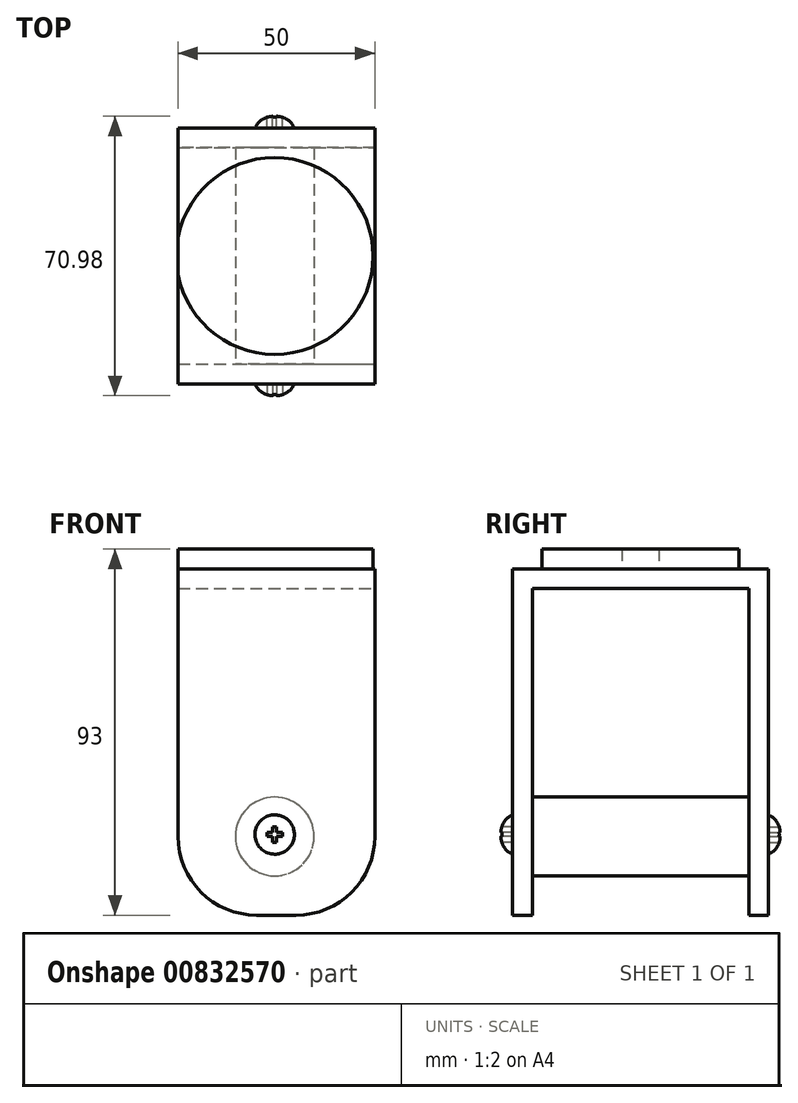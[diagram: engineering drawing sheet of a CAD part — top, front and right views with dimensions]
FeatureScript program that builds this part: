
annotation { "Feature Type Name" : "Feature", "Feature Type Description" : "" }
export const myFeature = defineFeature(function(context is Context, id is Id, definition is map)
    precondition{}
    {
        {
            var Q0;
            Q0=qCreatedBy(makeId("Front.planeOp"),FACE);
            var sketch = newSketch(context, id + "F0", { "sketchPlane" : qUnion([Q0])});
            skLineSegment(sketch, "E0.bottom", {"start": v(-24.56, 36.04) * mm, "end": v(25.44, 36.04) * mm});
            skLineSegment(sketch, "E0.top", {"start": v(-4.56, -46.96) * mm, "end": v(5.44, -46.96) * mm});
            skLineSegment(sketch, "E0.left", {"start": v(-24.56, 36.04) * mm, "end": v(-24.56, -26.96) * mm});
            skLineSegment(sketch, "E0.right", {"start": v(25.44, 36.04) * mm, "end": v(25.44, -26.96) * mm});
            skPoint(sketch, "E1.visualSharp", {"position": v(-24.56, -46.96) * mm});
            skArc(sketch, "E1.filletArc", {"start": v(-24.56, -26.96) * mm, "mid": v(-18.7, -41.1) * mm, "end": v(-4.56, -46.96) * mm});
            skPoint(sketch, "E2.visualSharp", {"position": v(25.44, -46.96) * mm});
            skArc(sketch, "E2.filletArc", {"start": v(5.44, -46.96) * mm, "mid": v(19.58, -41.1) * mm, "end": v(25.44, -26.96) * mm});
            skSolve(sketch);
        }
        {
            var Q0;
            Q0=makeQuery(id+"F0.imprint","IMPRINT",FACE,{"disambiguationData":[TD([[makeQuery(id+"F0.imprint","IMPRINT",EDGE,{"derivedFrom":sQuery(id+"F0.wireOp",EDGE,"E0.bottom")}),-1.0]])]});
            extrude(context, id + "F1", {"entities" : qUnion([Q0]), "depth" : 5 * mm, "offsetDistance" : 25 * mm});
        }
        {
            var Q0;
            Q0=makeQuery(id+"F1.opExtrude","SWEPT_FACE",FACE,{"disambiguationData":[OSD([sQuery(id+"F0.wireOp",EDGE,"E0.bottom")])]});
            var sketch = newSketch(context, id + "F2", { "sketchPlane" : qUnion([Q0])});
            skLineSegment(sketch, "E3.bottom", {"start": v(25.44, -5) * mm, "end": v(-24.56, -5) * mm});
            skLineSegment(sketch, "E3.top", {"start": v(25.44, 55) * mm, "end": v(-24.56, 55) * mm});
            skLineSegment(sketch, "E3.left", {"start": v(25.44, -5) * mm, "end": v(25.44, 55) * mm});
            skLineSegment(sketch, "E3.right", {"start": v(-24.56, -5) * mm, "end": v(-24.56, 55) * mm});
            skSolve(sketch);
        }
        {
            var Q0;
            {var subQ0=sQuery(id+"F2.wireOp",EDGE,"E3.top");Q0=makeQuery(id+"F2.imprint","IMPRINT",FACE,{"disambiguationData":[TD([[makeQuery(id+"F2.imprint","IMPRINT",EDGE,{"derivedFrom":subQ0}),1.0]])]});}
            var Q1;
            {var subQ0=sQuery(id+"F2.wireOp",EDGE,"E3.bottom");Q1=makeQuery(id+"F2.imprint","IMPRINT",FACE,{"disambiguationData":[TD([[makeQuery(id+"F2.imprint","IMPRINT",EDGE,{"derivedFrom":subQ0}),1.0]])]});}
            extrude(context, id + "F3", {"entities" : qUnion([Q0, Q1]), "operationType" : NewBodyOperationType.ADD, "depth" : 5 * mm, "offsetDistance" : 25 * mm});
        }
        {
            var Q0;
            Q0=makeQuery(id+"F1.opExtrude","CAP_FACE",FACE,{"disambiguationData":[OSD([sQuery(id+"F0.wireOp",EDGE,"E0.bottom"),sQuery(id+"F0.wireOp",EDGE,"E0.top"),sQuery(id+"F0.wireOp",EDGE,"E0.left"),sQuery(id+"F0.wireOp",EDGE,"E0.right"),sQuery(id+"F0.wireOp",EDGE,"E1.filletArc"),sQuery(id+"F0.wireOp",EDGE,"E2.filletArc")])],"isStart":true});
            cPlane(context, id + "F4", {"entities" : qUnion([Q0]), "cplaneType" : CPlaneType.OFFSET, "offset" : 27.5 * mm, "width" : 150 * mm, "height" : 150 * mm});
        }
        {
            var Q0;
            Q0=makeQuery(id+"F1.opExtrude","SWEPT_BODY",BODY,{"disambiguationData":[OSD([sQuery(id+"F0.wireOp",EDGE,"E0.bottom"),sQuery(id+"F0.wireOp",EDGE,"E0.top"),sQuery(id+"F0.wireOp",EDGE,"E0.left"),sQuery(id+"F0.wireOp",EDGE,"E0.right"),sQuery(id+"F0.wireOp",EDGE,"E1.filletArc"),sQuery(id+"F0.wireOp",EDGE,"E2.filletArc")])]});
            var Q1;
            Q1=qCreatedBy(id+"F4.planeOp",FACE);
            mirror(context, id + "F5", {"operationType" : NewBodyOperationType.ADD, "entities" : qUnion([Q0]), "mirrorPlane" : qUnion([Q1])});
        }
        {
            var Q0;
            {var subQ0=makeQuery(id+"F3.opExtrude","CAP_FACE",FACE,{"disambiguationData":[OSD([sQuery(id+"F2.wireOp",EDGE,"E3.bottom"),sQuery(id+"F2.wireOp",EDGE,"E3.top"),sQuery(id+"F2.wireOp",EDGE,"E3.left"),sQuery(id+"F2.wireOp",EDGE,"E3.right")])],"isStart":false});Q0=makeQuery(id+"F5.boolean.opBoolean","MERGE",FACE,{"derivedFrom":[subQ0,makeQuery(id+"F5.opPattern","COPY",FACE,{"derivedFrom":subQ0,"instanceName":"1"})]});}
            var sketch = newSketch(context, id + "F6", { "sketchPlane" : qUnion([Q0])});
            skCircle(sketch, "E4", {"center": v(0, 27.5) * mm, "radius": 25 * mm});
            skSolve(sketch);
        }
        {
            var Q0;
            {var subQ0=sQuery(id+"F6.wireOp",EDGE,"E4");var subQ1=makeQuery(id+"F3.opExtrude","CAP_EDGE",EDGE,{"disambiguationData":[OSD([sQuery(id+"F2.wireOp",EDGE,"E3.right")])],"isStart":false});var subQ2=makeQuery(id+"F5.boolean.opBoolean","MERGE",EDGE,{"derivedFrom":[subQ1,makeQuery(id+"F5.opPattern","COPY",EDGE,{"derivedFrom":subQ1,"instanceName":"1"})]});var subQ3=makeQuery(id+"F6.imprint","INTERSECT",VERTEX,{"disambiguationData":[OD(0.0)],"derivedFrom":[subQ2,subQ0]});Q0=makeQuery(id+"F6.imprint","IMPRINT",FACE,{"disambiguationData":[TD([[makeQuery(id+"F6.imprint","IMPRINT",EDGE,{"disambiguationData":[TD([[subQ3,-1.0]])],"derivedFrom":subQ0}),1.0]])]});}
            extrude(context, id + "F7", {"entities" : qUnion([Q0]), "operationType" : NewBodyOperationType.ADD, "depth" : 5 * mm, "offsetDistance" : 25 * mm});
        }
        {
            var Q0;
            Q0=makeQuery(id+"F1.opExtrude","CAP_FACE",FACE,{"disambiguationData":[OSD([sQuery(id+"F0.wireOp",EDGE,"E0.bottom"),sQuery(id+"F0.wireOp",EDGE,"E0.top"),sQuery(id+"F0.wireOp",EDGE,"E0.left"),sQuery(id+"F0.wireOp",EDGE,"E0.right"),sQuery(id+"F0.wireOp",EDGE,"E1.filletArc"),sQuery(id+"F0.wireOp",EDGE,"E2.filletArc")])],"isStart":true});
            var sketch = newSketch(context, id + "F8", { "sketchPlane" : qUnion([Q0])});
            skCircle(sketch, "E5", {"center": v(0, -26.97) * mm, "radius": 10 * mm});
            skSolve(sketch);
        }
        {
            var Q0;
            Q0=makeQuery(id+"F8.imprint","IMPRINT",FACE,{"disambiguationData":[TD([[makeQuery(id+"F8.imprint","IMPRINT",EDGE,{"derivedFrom":sQuery(id+"F8.wireOp",EDGE,"E5")}),1.0]])]});
            extrude(context, id + "F9", {"entities" : qUnion([Q0]), "operationType" : NewBodyOperationType.ADD, "endBound" : BoundingType.UP_TO_NEXT, "depth" : 25 * mm, "offsetDistance" : 25 * mm});
        }
        {
            var Q0;
            Q0=makeQuery(id+"F3.boolean.opBoolean","MERGE",FACE,{"derivedFrom":[makeQuery(id+"F1.opExtrude","CAP_FACE",FACE,{"disambiguationData":[OSD([sQuery(id+"F0.wireOp",EDGE,"E0.bottom"),sQuery(id+"F0.wireOp",EDGE,"E0.top"),sQuery(id+"F0.wireOp",EDGE,"E0.left"),sQuery(id+"F0.wireOp",EDGE,"E0.right"),sQuery(id+"F0.wireOp",EDGE,"E1.filletArc"),sQuery(id+"F0.wireOp",EDGE,"E2.filletArc")])],"isStart":false}),makeQuery(id+"F3.opExtrude","SWEPT_FACE",FACE,{"disambiguationData":[OSD([sQuery(id+"F2.wireOp",EDGE,"E3.bottom")])]})]});
            var sketch = newSketch(context, id + "F10", { "sketchPlane" : qUnion([Q0])});
            skCircle(sketch, "E6", {"center": v(0, -26.47) * mm, "radius": 5 * mm});
            skSolve(sketch);
        }
        {
            var Q0;
            Q0=makeQuery(id+"F10.imprint","IMPRINT",FACE,{"disambiguationData":[TD([[makeQuery(id+"F10.imprint","IMPRINT",EDGE,{"derivedFrom":sQuery(id+"F10.wireOp",EDGE,"E6")}),1.0]])]});
            extrude(context, id + "F11", {"entities" : qUnion([Q0]), "operationType" : NewBodyOperationType.ADD, "depth" : 3 * mm, "offsetDistance" : 25 * mm});
        }
        {
            var Q0;
            Q0=makeQuery(id+"F11.opExtrude","CAP_FACE",FACE,{"disambiguationData":[OSD([sQuery(id+"F10.wireOp",EDGE,"E6")])],"isStart":false});
            var sketch = newSketch(context, id + "F12", { "sketchPlane" : qUnion([Q0])});
            skPoint(sketch, "E7.oppositeSnap0", {"position": v(1, -26.47) * mm});
            skLineSegment(sketch, "E8.bottom", {"start": v(-2, -25.97) * mm, "end": v(1, -25.97) * mm});
            skLineSegment(sketch, "E8.top", {"start": v(-2, -26.97) * mm, "end": v(1, -26.97) * mm});
            skLineSegment(sketch, "E8.left", {"start": v(-2, -25.97) * mm, "end": v(-2, -26.97) * mm});
            skLineSegment(sketch, "E8.right", {"start": v(2, -25.97) * mm, "end": v(2, -26.97) * mm});
            skLineSegment(sketch, "E9.trimOffspring", {"start": v(1, -25.97) * mm, "end": v(2, -25.97) * mm});
            skLineSegment(sketch, "E10.trimOffspring", {"start": v(1, -26.97) * mm, "end": v(2, -26.97) * mm});
            skLineSegment(sketch, "E11.bottom", {"start": v(-0.5, -24.47) * mm, "end": v(0.5, -24.47) * mm});
            skLineSegment(sketch, "E11.top", {"start": v(-0.5, -28.47) * mm, "end": v(0.5, -28.47) * mm});
            skLineSegment(sketch, "E11.left", {"start": v(-0.5, -24.47) * mm, "end": v(-0.5, -28.47) * mm});
            skLineSegment(sketch, "E11.right", {"start": v(0.5, -24.47) * mm, "end": v(0.5, -28.47) * mm});
            skSolve(sketch);
        }
        {
            var Q0;
            Q0=makeQuery(id+"F11.opExtrude","CAP_EDGE",EDGE,{"disambiguationData":[OSD([sQuery(id+"F10.wireOp",EDGE,"E6")])],"isStart":false});
            fillet(context, id + "F13", {"entities" : qUnion([Q0]), "radius" : 5 * mm, "tangentPropagation" : true, "allowEdgeOverflow" : false});
        }
        {
            var Q0;
            {var subQ0=sQuery(id+"F12.wireOp",EDGE,"E8.left");Q0=makeQuery(id+"F12.imprint","IMPRINT",FACE,{"disambiguationData":[TD([[makeQuery(id+"F12.imprint","IMPRINT",EDGE,{"derivedFrom":subQ0}),1.0]])]});}
            var Q1;
            Q1=makeQuery(id+"F12.imprint","IMPRINT",FACE,{"disambiguationData":[TD([[makeQuery(id+"F12.imprint","IMPRINT",EDGE,{"derivedFrom":sQuery(id+"F12.wireOp",EDGE,"E8.right")}),-1.0]])]});
            var Q2;
            {var subQ0=sQuery(id+"F12.wireOp",EDGE,"E11.left");var subQ1=sQuery(id+"F12.wireOp",EDGE,"E8.bottom");var subQ2=makeQuery(id+"F12.imprint","INTERSECT",VERTEX,{"derivedFrom":[subQ1,subQ0]});Q2=makeQuery(id+"F12.imprint","IMPRINT",FACE,{"disambiguationData":[TD([[makeQuery(id+"F12.imprint","IMPRINT",EDGE,{"disambiguationData":[TD([[subQ2,-1.0]])],"derivedFrom":subQ1}),-1.0]])]});}
            var Q3;
            {var subQ5=sQuery(id+"F12.wireOp",EDGE,"E11.bottom");Q3=makeQuery(id+"F12.imprint","IMPRINT",FACE,{"disambiguationData":[TD([[makeQuery(id+"F12.imprint","IMPRINT",EDGE,{"derivedFrom":subQ5}),-1.0]])]});}
            var Q4;
            {var subQ5=sQuery(id+"F12.wireOp",EDGE,"E11.top");Q4=makeQuery(id+"F12.imprint","IMPRINT",FACE,{"disambiguationData":[TD([[makeQuery(id+"F12.imprint","IMPRINT",EDGE,{"derivedFrom":subQ5}),1.0]])]});}
            extrude(context, id + "F14", {"entities" : qUnion([Q0, Q1, Q2, Q3, Q4]), "operationType" : NewBodyOperationType.REMOVE, "oppositeDirection" : true, "depth" : 3 * mm, "offsetDistance" : 25 * mm});
        }
        {
            var Q0;
            Q0=makeQuery(id+"F5.opPattern","COPY",FACE,{"derivedFrom":makeQuery(id+"F3.boolean.opBoolean","MERGE",FACE,{"derivedFrom":[makeQuery(id+"F1.opExtrude","CAP_FACE",FACE,{"disambiguationData":[OSD([sQuery(id+"F0.wireOp",EDGE,"E0.bottom"),sQuery(id+"F0.wireOp",EDGE,"E0.top"),sQuery(id+"F0.wireOp",EDGE,"E0.left"),sQuery(id+"F0.wireOp",EDGE,"E0.right"),sQuery(id+"F0.wireOp",EDGE,"E1.filletArc"),sQuery(id+"F0.wireOp",EDGE,"E2.filletArc")])],"isStart":false}),makeQuery(id+"F3.opExtrude","SWEPT_FACE",FACE,{"disambiguationData":[OSD([sQuery(id+"F2.wireOp",EDGE,"E3.bottom")])]})]}),"instanceName":"1"});
            var sketch = newSketch(context, id + "F15", { "sketchPlane" : qUnion([Q0])});
            skCircle(sketch, "E12", {"center": v(0, -26.47) * mm, "radius": 5 * mm});
            skSolve(sketch);
        }
        {
            var Q0;
            Q0=makeQuery(id+"F15.imprint","IMPRINT",FACE,{"disambiguationData":[TD([[makeQuery(id+"F15.imprint","IMPRINT",EDGE,{"derivedFrom":sQuery(id+"F15.wireOp",EDGE,"E12")}),1.0]])]});
            extrude(context, id + "F16", {"entities" : qUnion([Q0]), "operationType" : NewBodyOperationType.ADD, "depth" : 3 * mm, "offsetDistance" : 25 * mm});
        }
        {
            var Q0;
            Q0=makeQuery(id+"F16.opExtrude","CAP_FACE",FACE,{"disambiguationData":[OSD([sQuery(id+"F15.wireOp",EDGE,"E12")])],"isStart":false});
            var sketch = newSketch(context, id + "F17", { "sketchPlane" : qUnion([Q0])});
            skLineSegment(sketch, "E13.bottom", {"start": v(-0.5, -24.47) * mm, "end": v(0.5, -24.47) * mm});
            skLineSegment(sketch, "E13.top", {"start": v(-0.5, -28.47) * mm, "end": v(0.5, -28.47) * mm});
            skLineSegment(sketch, "E13.left", {"start": v(-0.5, -24.47) * mm, "end": v(-0.5, -25.97) * mm});
            skLineSegment(sketch, "E13.right", {"start": v(0.5, -24.47) * mm, "end": v(0.5, -25.97) * mm});
            skLineSegment(sketch, "E14.bottom", {"start": v(-2, -25.97) * mm, "end": v(-0.5, -25.97) * mm});
            skLineSegment(sketch, "E14.top", {"start": v(-2, -26.97) * mm, "end": v(-0.5, -26.97) * mm});
            skLineSegment(sketch, "E14.left", {"start": v(-2, -25.97) * mm, "end": v(-2, -26.97) * mm});
            skLineSegment(sketch, "E14.right", {"start": v(2, -25.97) * mm, "end": v(2, -26.97) * mm});
            skLineSegment(sketch, "E15.trimOffspring", {"start": v(0.5, -25.97) * mm, "end": v(2, -25.97) * mm});
            skLineSegment(sketch, "E16.trimOffspring", {"start": v(-0.5, -26.97) * mm, "end": v(-0.5, -28.47) * mm});
            skLineSegment(sketch, "E17.trimOffspring", {"start": v(0.5, -26.97) * mm, "end": v(0.5, -28.47) * mm});
            skLineSegment(sketch, "E18.trimOffspring", {"start": v(0.5, -26.97) * mm, "end": v(2, -26.97) * mm});
            skSolve(sketch);
        }
        {
            var Q0;
            Q0=makeQuery(id+"F17.imprint","IMPRINT",FACE,{"disambiguationData":[TD([[makeQuery(id+"F17.imprint","IMPRINT",EDGE,{"derivedFrom":sQuery(id+"F17.wireOp",EDGE,"E13.bottom")}),-1.0]])]});
            extrude(context, id + "F18", {"entities" : qUnion([Q0]), "operationType" : NewBodyOperationType.REMOVE, "oppositeDirection" : true, "depth" : 3 * mm, "offsetDistance" : 25 * mm});
        }
        {
            var Q0;
            Q0=makeQuery(id+"F16.opExtrude","CAP_EDGE",EDGE,{"disambiguationData":[OSD([sQuery(id+"F15.wireOp",EDGE,"E12")])],"isStart":false});
            fillet(context, id + "F19", {"entities" : qUnion([Q0]), "radius" : 5 * mm, "tangentPropagation" : true, "allowEdgeOverflow" : false});
        }
    });
